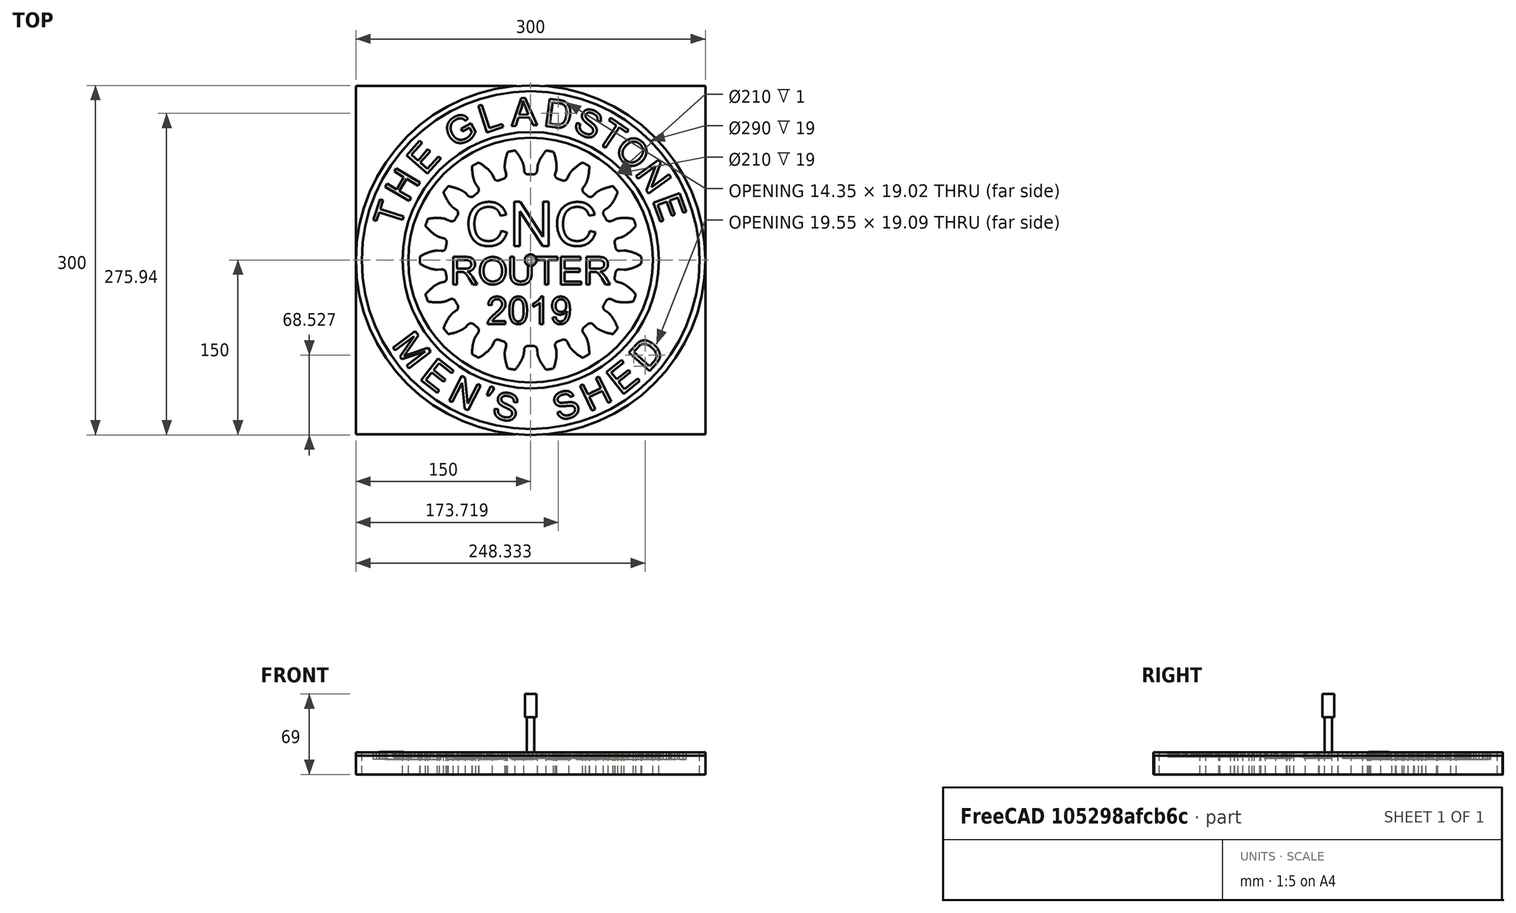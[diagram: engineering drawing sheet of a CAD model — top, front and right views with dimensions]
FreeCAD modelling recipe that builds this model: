
FCSTD DOCUMENT  (FreeCAD 0.19RUnknown)
Label: Final Men's shed drawing
License: All rights reserved
LicenseURL: http://en.wikipedia.org/wiki/All_rights_reserved
objects: Part::Part2DObjectPython×27, Part::Extrusion×23, Part::FeaturePython×6, PartDesign::Body×4, App::DocumentObjectGroup×4, PartDesign::Pocket×3, Part::Cylinder×2, Path::FeaturePython×2, Part::Cut×1, PartDesign::Pad×1, Path::FeatureCompoundPython×1, App::FeaturePython×1
note: 71 computed .brp shape members not serialized (recipe doc carries the construction recipe); baked Part::Feature solids carry a one-line shape summary decoded from their .brp

FEATURE [Part::Cylinder] Cylinder
  Angle = 360
  AttacherType = Attacher::AttachEngine3D
  Height = 16
  Radius = 150
FEATURE [Part::FeaturePython] Tube  # WARN: FeaturePython — macro-defined, semantics opaque (R4)
  AttacherType = Attacher::AttachEngine3D
  Height = 19
  InnerRadius = 145
  OuterRadius = 150
  Placement = pos=(0,0,-19) rot=(0,0,1;0rad)
FEATURE [Part::FeaturePython] Tube001  # WARN: FeaturePython — macro-defined, semantics opaque (R4)
  AttacherType = Attacher::AttachEngine3D
  Height = 19
  InnerRadius = 105
  OuterRadius = 110
  Placement = pos=(0,0,-19) rot=(0,0,1;0rad)
FEATURE [Part::Cylinder] Cylinder001
  Angle = 360
  AttacherType = Attacher::AttachEngine3D
  Height = 5
  Placement = pos=(0,0,15) rot=(0,0,1;0rad)
  Radius = 105
FEATURE [Part::Cut] Cut
  Base = -> Cylinder
  Placement = pos=(0,0,-19) rot=(0,0,1;0rad)
  Tool = -> Cylinder001
FEATURE [Part::Part2DObjectPython] InvoluteGear  # Draft 2D object (typed FeaturePython)
  ExternalGear = true
  HighPrecision = true
  Modules = 9.5
  NumberOfTeeth = 18
  PressureAngle = 20
FEATURE [PartDesign::Pad] Pad
  Direction = (1,1,1)
  Length = 19
  Length2 = 100
  Profile = -> InvoluteGear
  Type = 0
FEATURE [Part::Part2DObjectPython] ShapeString  # Draft 2D object (typed FeaturePython)
  FontFile = <path>
  Placement = pos=(-56,12,19) rot=(0,0,1;0rad)
  Size = 40
  String = CNC
  Tracking = 0
FEATURE [Part::Part2DObjectPython] ShapeString001  # Draft 2D object (typed FeaturePython)
  FontFile = <path>
  Placement = pos=(-69,-21,19) rot=(0,0,1;0rad)
  Size = 25
  String = ROUTER
  Tracking = 0
FEATURE [Part::Part2DObjectPython] ShapeString002  # Draft 2D object (typed FeaturePython)
  FontFile = <path>
  Placement = pos=(-38,-55,19) rot=(0,0,1;0rad)
  Size = 25
  String = 2019
  Tracking = 0
FEATURE [PartDesign::Pocket] Pocket
  BaseFeature = -> Pad
  Length = 5
  Length2 = 100
  Profile = -> ShapeString
  Type = 0
FEATURE [PartDesign::Pocket] Pocket001
  BaseFeature = -> Pocket
  Length = 5
  Length2 = 100
  Profile = -> ShapeString001
  Type = 0
FEATURE [PartDesign::Pocket] Pocket002
  BaseFeature = -> Pocket001
  Length = 5
  Length2 = 100
  Profile = -> ShapeString002
  Type = 0
FEATURE [PartDesign::Body] Body
  Group = -> [InvoluteGear,Pad,ShapeString,ShapeString001,ShapeString002,Pocket,Pocket001,Pocket002]
  Origin = -> Origin
  Placement = pos=(0,0,-19) rot=(0,0,1;0rad)
  Tip = -> Pocket002
FEATURE [PartDesign::Body] Body001
  Origin = -> Origin001
FEATURE [Part::Part2DObjectPython] ShapeString003  label="E"  # Draft 2D object (typed FeaturePython)
  FontFile = <path>
  Size = 25
  String = E
  Tracking = 0
FEATURE [Part::Extrusion] Extrusion  label="E001"
  Base = -> ShapeString003
  Dir = (0,0,6)
  DirMode = 0
  FaceMakerClass = Part::FaceMakerBullseye
  LengthFwd = 0
  LengthRev = 0
  Placement = pos=(104.496,51.7768,-6) rot=(0,0,-1;1.22173rad)
  Solid = false
  Symmetric = false
FEATURE [Part::Part2DObjectPython] ShapeString004  label="N"  # Draft 2D object (typed FeaturePython)
  FontFile = <path>
  Size = 25
  String = N
  Tracking = 0
FEATURE [Part::Extrusion] Extrusion001  label="N001"
  Base = -> ShapeString004
  Dir = (0,0,6)
  DirMode = 0
  FaceMakerClass = Part::FaceMakerBullseye
  LengthFwd = 0
  LengthRev = 0
  Placement = pos=(89.0208,74.1709,-6) rot=(0,0,-1;0.945096rad)
  Solid = false
  Symmetric = false
FEATURE [Part::Part2DObjectPython] ShapeString005  label="O"  # Draft 2D object (typed FeaturePython)
  FontFile = <path>
  Size = 25
  String = O
  Tracking = 0
FEATURE [Part::Extrusion] Extrusion002  label="O001"
  Base = -> ShapeString005
  Dir = (0,0,6)
  DirMode = 0
  FaceMakerClass = Part::FaceMakerBullseye
  LengthFwd = 0
  LengthRev = 0
  Placement = pos=(70.2591,92.8652,-6) rot=(0,0,-1;0.755902rad)
  Solid = false
  Symmetric = false
FEATURE [Part::Part2DObjectPython] ShapeString006  label="T"  # Draft 2D object (typed FeaturePython)
  FontFile = <path>
  Size = 25
  String = T
  Tracking = 0
FEATURE [Part::Extrusion] Extrusion003  label="T001"
  Base = -> ShapeString006
  Dir = (0,0,6)
  DirMode = 0
  FaceMakerClass = Part::FaceMakerBullseye
  LengthFwd = 0
  LengthRev = 0
  Placement = pos=(54.7512,103.042,-6) rot=(0,0,-1;0.60144rad)
  Solid = false
  Symmetric = false
FEATURE [Part::Part2DObjectPython] ShapeString007  label="S"  # Draft 2D object (typed FeaturePython)
  FontFile = <path>
  Size = 25
  String = S
  Tracking = 0
FEATURE [Part::Extrusion] Extrusion004  label="S001"
  Base = -> ShapeString007
  Dir = (0,0,6)
  DirMode = 0
  FaceMakerClass = Part::FaceMakerBullseye
  LengthFwd = 0
  LengthRev = 0
  Placement = pos=(35.117,111.121,-6) rot=(0,0,-1;0.4297rad)
  Solid = false
  Symmetric = false
FEATURE [Part::Part2DObjectPython] ShapeString008  label="D"  # Draft 2D object (typed FeaturePython)
  FontFile = <path>
  Size = 25
  String = D
  Tracking = 0
FEATURE [Part::Extrusion] Extrusion005  label="D001"
  Base = -> ShapeString008
  Dir = (0,0,6)
  DirMode = 0
  FaceMakerClass = Part::FaceMakerBullseye
  LengthFwd = 0
  LengthRev = 0
  Placement = pos=(10.6216,115.34,-6) rot=(0,0,-1;0.135612rad)
  Solid = false
  Symmetric = false
FEATURE [Part::Part2DObjectPython] ShapeString009  label="A"  # Draft 2D object (typed FeaturePython)
  FontFile = <path>
  Size = 25
  String = A
  Tracking = 0
FEATURE [Part::Extrusion] Extrusion006  label="A001"
  Base = -> ShapeString009
  Dir = (0,0,6)
  DirMode = 0
  FaceMakerClass = Part::FaceMakerBullseye
  LengthFwd = 0
  LengthRev = 0
  Placement = pos=(-16.1998,115.11,-6) rot=(0,0,1;0.036303rad)
  Solid = false
  Symmetric = false
FEATURE [Part::Part2DObjectPython] ShapeString010  label="L"  # Draft 2D object (typed FeaturePython)
  FontFile = <path>
  Size = 25
  String = L
  Tracking = 0
FEATURE [Part::Extrusion] Extrusion007  label="L001"
  Base = -> ShapeString010
  Dir = (0,0,6)
  DirMode = 0
  FaceMakerClass = Part::FaceMakerBullseye
  LengthFwd = 0
  LengthRev = 0
  Placement = pos=(-39.8354,108.974,-6) rot=(0,0,1;0.312763rad)
  Solid = false
  Symmetric = false
FEATURE [Part::Part2DObjectPython] ShapeString011  label="G"  # Draft 2D object (typed FeaturePython)
  FontFile = <path>
  Size = 25
  String = G
  Tracking = 0
FEATURE [Part::Extrusion] Extrusion008  label="G001"
  Base = -> ShapeString011
  Dir = (0,0,6)
  DirMode = 0
  FaceMakerClass = Part::FaceMakerBullseye
  LengthFwd = 0
  LengthRev = 0
  Placement = pos=(-65.8185,95.6443,-6) rot=(0,0,1;0.502131rad)
  Solid = false
  Symmetric = false
FEATURE [Part::Part2DObjectPython] ShapeString012  label=" "  # Draft 2D object (typed FeaturePython)
  FontFile = <path>
  Size = 25
  Tracking = 0
FEATURE [Part::Extrusion] Extrusion009  label=" 001"
  Base = -> ShapeString012
  Dir = (0,0,6)
  DirMode = 0
  FaceMakerClass = Part::FaceMakerBullseye
  LengthFwd = 0
  LengthRev = 0
  Placement = pos=(-58.6434,99.0983,0) rot=(0,0,1;0.44708rad)
  Solid = false
  Symmetric = false
FEATURE [Part::Part2DObjectPython] ShapeString013  label="E002"  # Draft 2D object (typed FeaturePython)
  FontFile = <path>
  Size = 25
  String = E
  Tracking = 0
FEATURE [Part::Extrusion] Extrusion010  label="E003"
  Base = -> ShapeString013
  Dir = (0,0,6)
  DirMode = 0
  FaceMakerClass = Part::FaceMakerBullseye
  LengthFwd = 0
  LengthRev = 0
  Placement = pos=(-90.3603,72.2492,-6) rot=(0,0,1;0.845787rad)
  Solid = false
  Symmetric = false
FEATURE [Part::Part2DObjectPython] ShapeString014  label="H"  # Draft 2D object (typed FeaturePython)
  FontFile = <path>
  Size = 25
  String = H
  Tracking = 0
FEATURE [Part::Extrusion] Extrusion011  label="H001"
  Base = -> ShapeString014
  Dir = (0,0,6)
  DirMode = 0
  FaceMakerClass = Part::FaceMakerBullseye
  LengthFwd = 0
  LengthRev = 0
  Placement = pos=(-105.725,48.6335,-6) rot=(0,0,1;1.03516rad)
  Solid = false
  Symmetric = false
FEATURE [Part::Part2DObjectPython] ShapeString015  label="T002"  # Draft 2D object (typed FeaturePython)
  FontFile = <path>
  Size = 25
  String = T
  Tracking = 0
FEATURE [Part::Extrusion] Extrusion012  label="T003"
  Base = -> ShapeString015
  Dir = (0,0,6)
  DirMode = 0
  FaceMakerClass = Part::FaceMakerBullseye
  LengthFwd = 0
  LengthRev = 0
  Placement = pos=(-112.507,26.6229,-6) rot=(0.008726,-0.011977,0.99989;1.25936rad)
  Solid = false
  Symmetric = false
FEATURE [App::DocumentObjectGroup] FcString_THE_GLADST
  Group = -> [ShapeString003,Extrusion,ShapeString004,Extrusion001,ShapeString005,Extrusion002,ShapeString006,Extrusion003,ShapeString007,Extrusion004,ShapeString008,Extrusion005,ShapeString009,Extrusion006,ShapeString010,Extrusion007,ShapeString011,Extrusion008,ShapeString012,Extrusion009,ShapeString013,Extrusion010,ShapeString014,Extrusion011,ShapeString015,Extrusion012]
FEATURE [PartDesign::Body] Body002
  Origin = -> Origin002
FEATURE [PartDesign::Body] Body003
  Origin = -> Origin003
FEATURE [Part::Part2DObjectPython] ShapeString016  label="M"  # Draft 2D object (typed FeaturePython)
  FontFile = <path>
  Size = 25
  String = M
  Tracking = 0
FEATURE [Part::Extrusion] Extrusion013  label="M001"
  Base = -> ShapeString016
  Dir = (0,0,4)
  DirMode = 0
  FaceMakerClass = Part::FaceMakerBullseye
  LengthFwd = 0
  LengthRev = 0
  Placement = pos=(-119.53,-73.22,-4) rot=(0,0,-1;0.925025rad)
  Solid = false
  Symmetric = false
FEATURE [Part::Part2DObjectPython] ShapeString017  label="E004"  # Draft 2D object (typed FeaturePython)
  FontFile = <path>
  Size = 25
  String = E
  Tracking = 0
FEATURE [Part::Extrusion] Extrusion014  label="E005"
  Base = -> ShapeString017
  Dir = (0,0,4)
  DirMode = 0
  FaceMakerClass = Part::FaceMakerBullseye
  LengthFwd = 0
  LengthRev = 0
  Placement = pos=(-96.02,-101.65,-4) rot=(0,0,-1;0.663225rad)
  Solid = false
  Symmetric = false
FEATURE [Part::Part2DObjectPython] ShapeString018  label="N002"  # Draft 2D object (typed FeaturePython)
  FontFile = <path>
  Size = 25
  String = N
  Tracking = 0
FEATURE [Part::Extrusion] Extrusion015  label="N003"
  Base = -> ShapeString018
  Dir = (0,0,4)
  DirMode = 0
  FaceMakerClass = Part::FaceMakerBullseye
  LengthFwd = 0
  LengthRev = 0
  Placement = pos=(-72.27,-119.5,-4) rot=(0,0,-1;0.471239rad)
  Solid = false
  Symmetric = false
FEATURE [Part::Part2DObjectPython] ShapeString019  label="'"  # Draft 2D object (typed FeaturePython)
  FontFile = <path>
  Size = 25
  String = '
  Tracking = 0
FEATURE [Part::Extrusion] Extrusion016  label="'001"
  Base = -> ShapeString019
  Dir = (0,0,4)
  DirMode = 0
  FaceMakerClass = Part::FaceMakerBullseye
  LengthFwd = 0
  LengthRev = 0
  Placement = pos=(-47,-128.4,-4) rot=(0,0,-1;0.506145rad)
  Solid = false
  Symmetric = false
FEATURE [Part::Part2DObjectPython] ShapeString020  label="S002"  # Draft 2D object (typed FeaturePython)
  FontFile = <path>
  Size = 25
  String = S
  Tracking = 0
FEATURE [Part::Extrusion] Extrusion017  label="S003"
  Base = -> ShapeString020
  Dir = (0,0,4)
  DirMode = 0
  FaceMakerClass = Part::FaceMakerBullseye
  LengthFwd = 0
  LengthRev = 0
  Placement = pos=(-34,-135.13,-4) rot=(0,0,-1;0.20944rad)
  Solid = false
  Symmetric = false
FEATURE [Part::Part2DObjectPython] ShapeString021  label=" 002"  # Draft 2D object (typed FeaturePython)
  FontFile = <path>
  Size = 25
  Tracking = 0
FEATURE [Part::Extrusion] Extrusion018  label=" 003"
  Base = -> ShapeString021
  Dir = (0,0,4)
  DirMode = 0
  FaceMakerClass = Part::FaceMakerBullseye
  LengthFwd = 0
  LengthRev = 0
  Placement = pos=(23.941,-112.634,0) rot=(0,0,1;3.1765rad)
  Solid = false
  Symmetric = false
FEATURE [Part::Part2DObjectPython] ShapeString022  label="S004"  # Draft 2D object (typed FeaturePython)
  FontFile = <path>
  Size = 25
  String = S
  Tracking = 0
FEATURE [Part::Extrusion] Extrusion019  label="S005"
  Base = -> ShapeString022
  Dir = (0,0,4)
  DirMode = 0
  FaceMakerClass = Part::FaceMakerBullseye
  LengthFwd = 0
  LengthRev = 0
  Placement = pos=(23.99,-139,-4) rot=(0,0,1;0.331613rad)
  Solid = false
  Symmetric = false
FEATURE [Part::Part2DObjectPython] ShapeString023  label="H002"  # Draft 2D object (typed FeaturePython)
  FontFile = <path>
  Size = 25
  String = H
  Tracking = 0
FEATURE [Part::Extrusion] Extrusion020  label="H003"
  Base = -> ShapeString023
  Dir = (0,0,4)
  DirMode = 0
  FaceMakerClass = Part::FaceMakerBullseye
  LengthFwd = 0
  LengthRev = 0
  Placement = pos=(50.39,-130.46,-4) rot=(0,0,1;0.453786rad)
  Solid = false
  Symmetric = false
FEATURE [Part::Part2DObjectPython] ShapeString024  label="E006"  # Draft 2D object (typed FeaturePython)
  FontFile = <path>
  Size = 25
  String = E
  Tracking = 0
FEATURE [Part::Extrusion] Extrusion021  label="E007"
  Base = -> ShapeString024
  Dir = (0,0,4)
  DirMode = 0
  FaceMakerClass = Part::FaceMakerBullseye
  LengthFwd = 0
  LengthRev = 0
  Placement = pos=(78,-116.42,-4) rot=(0,0,1;0.680678rad)
  Solid = false
  Symmetric = false
FEATURE [Part::Part2DObjectPython] ShapeString025  label="D002"  # Draft 2D object (typed FeaturePython)
  FontFile = <path>
  Size = 25
  String = D
  Tracking = 0
FEATURE [Part::Extrusion] Extrusion022  label="D003"
  Base = -> ShapeString025
  Dir = (0,0,4)
  DirMode = 0
  FaceMakerClass = Part::FaceMakerBullseye
  LengthFwd = 0
  LengthRev = 0
  Placement = pos=(100.46,-97,-4) rot=(0,0,1;0.837758rad)
  Solid = false
  Symmetric = false
FEATURE [App::DocumentObjectGroup] FcString_DEHS_S_NEM
  Group = -> [ShapeString016,Extrusion013,ShapeString017,Extrusion014,ShapeString018,Extrusion015,ShapeString019,Extrusion016,ShapeString020,Extrusion017,ShapeString021,Extrusion018,ShapeString022,Extrusion019,ShapeString023,Extrusion020,ShapeString024,Extrusion021,ShapeString025,Extrusion022]
FEATURE [Path::FeatureCompoundPython] Operations  # Path/CAM operation (typed FeaturePython)
  UsePlacements = false
FEATURE [App::FeaturePython] SetupSheet  # Path/CAM operation (typed FeaturePython)
  ClearanceHeightExpression = OpStockZMax+SetupSheet.ClearanceHeightOffset
  ClearanceHeightOffset = 5
  CoolantMode = 0
  CoolantModes = None | Flood | Mist
  FinalDepthExpression = OpFinalDepth
  HorizRapid = 0
  SafeHeightExpression = OpStockZMax+SetupSheet.SafeHeightOffset
  SafeHeightOffset = 3
  StartDepthExpression = OpStartDepth
  StepDownExpression = OpToolDiameter
  VertRapid = 0
FEATURE [Part::FeaturePython] Clone  label="Model-Cut"  # Draft clone (typed FeaturePython)
  AttacherType = Attacher::AttachEngine3D
  Fuse = false
  Objects = -> [Cut]
  PathResource = Model
  Placement = pos=(0,0,-19) rot=(0,0,1;0rad)
  Scale = (1,1,1)
FEATURE [App::DocumentObjectGroup] Model
  Group = -> [Clone]
FEATURE [Part::FeaturePython] Stock001  # WARN: FeaturePython — macro-defined, semantics opaque (R4)
  Height = 16
  Length = 300
  Placement = pos=(-150,-149.488,-19) rot=(0,0,1;0rad)
  StockType = CreateBox
  Width = 298.975
FEATURE [Part::FeaturePython] ToolBit001  label="6.4mm Endmill"  # Path/CAM toolbit (typed FeaturePython)
  BitPropertyNames = Chipload | CuttingEdgeHeight | Diameter | Flutes | Length | Material | ShankDiameter
  BitShape = <path>
  Chipload = 0
  CuttingEdgeHeight = 30
  Diameter = 6.4
  File = <userpath>/MensShed/CNCRouter/FreeCAD/Bit/6.4mm_Endmill.fctb
  Flutes = 0
  Length = 50
  Material = 0
  ShankDiameter = 10
  ShapeName = endmill
FEATURE [Part::FeaturePython] ToolBit  label="6.4mm Endmill002"  # Path/CAM toolbit (typed FeaturePython)
  BitPropertyNames = Chipload | CuttingEdgeHeight | Diameter | Flutes | Length | Material | ShankDiameter
  BitShape = <path>
  Chipload = 0
  CuttingEdgeHeight = 30
  Diameter = 6.4
  Flutes = 0
  Length = 50
  Material = 0
  ShankDiameter = 10
  ShapeName = endmill
FEATURE [Path::FeaturePython] __4mm_Endmill  label="6.4mm Endmill001"  # Path/CAM operation (typed FeaturePython)
  HorizFeed = 20
  HorizRapid = 0
  SpindleDir = 0
  SpindleSpeed = 1
  Tool = -> ToolBit
  ToolNumber = 2
  VertFeed = 20
  VertRapid = 0
  expr: HorizRapid = SetupSheet.HorizRapid
  expr: VertRapid = SetupSheet.VertRapid
FEATURE [App::DocumentObjectGroup] Tools
  Group = -> [__4mm_Endmill]
FEATURE [Path::FeaturePython] Job  # Path/CAM operation (typed FeaturePython)
  CycleTime = 00:00:00
  Fixtures = G54
  GeometryTolerance = 0.01
  Model = -> Model
  Operations = -> Operations
  OrderOutputBy = 0
  PostProcessor = 7
  PostProcessorOutputFile = %D/%d.ngc
  SetupSheet = -> SetupSheet
  SplitOutput = false
  Stock = -> Stock001
  Tools = -> Tools
note: 28 file-system paths scrubbed to <path> (originals preserved in the JSON sidecar)
